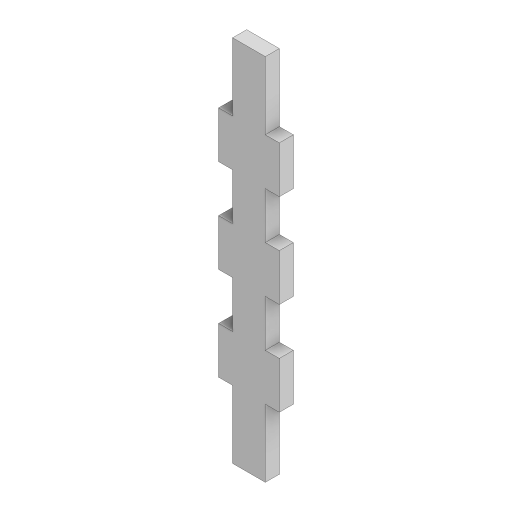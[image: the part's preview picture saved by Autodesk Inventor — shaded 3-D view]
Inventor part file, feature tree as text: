
AUTODESK INVENTOR PART (.ipt)
format: ipt  version: 2023.3 (Build 273359000, 359)  size: 128,000 bytes
history: native  units: mm
features: extrude x1, sketch x1
ambient origin geometry x8: Origin, YZ Plane, XZ Plane, XY Plane, X Axis, Y Axis, Z Axis, Center Point
bodies: Solid1 (feature_tree)
feature tree (2):
  extrude  "Extrusion1"  Depth=13.0mm
  sketch  "Sketch1"  dims[d0=79.0mm d1=13.0mm d2=3.0mm d3=3.0mm d4=3.0mm d5=10.0mm d6=4.0mm d7=10.0mm d9=3.0mm d10=0.0mm d11=10.0mm]
